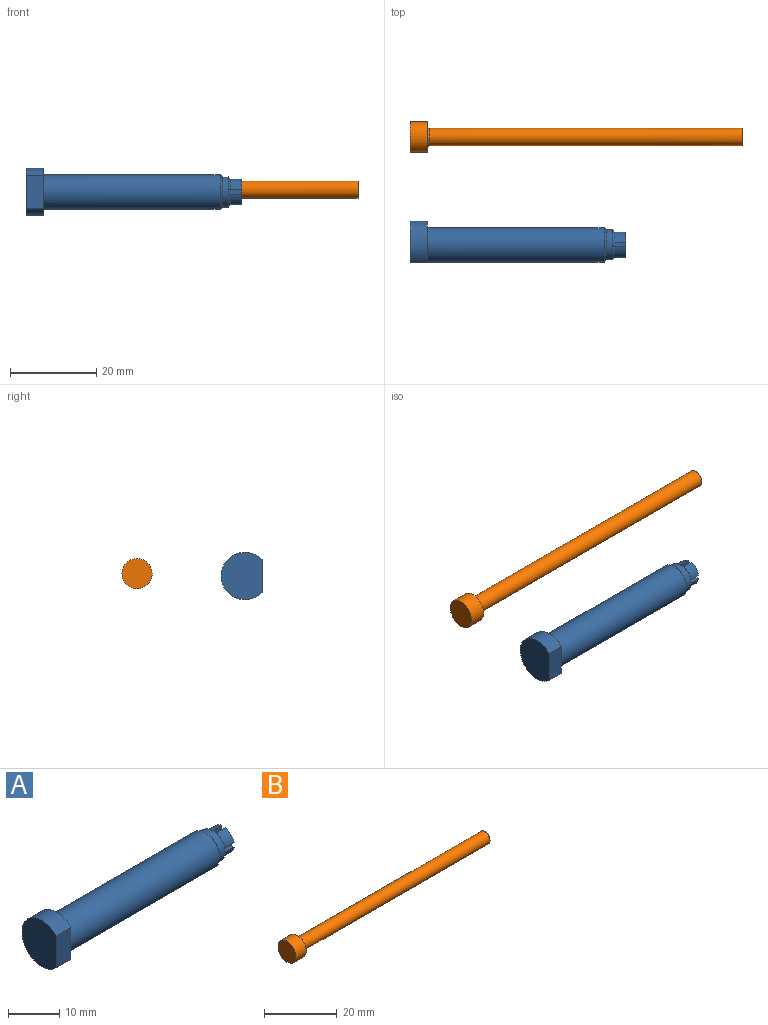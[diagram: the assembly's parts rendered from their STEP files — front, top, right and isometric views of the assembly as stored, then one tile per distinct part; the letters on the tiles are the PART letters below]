
ASSEMBLY  parts=2 mates=1
PART A: 32 faces, bbox 50x9.5x11 mm
  f0: cone r=3mm half-angle=45deg, axis (-1,0,0), area 2.9mm2, adj f1,f11,f21,f28
  f1: cylinder r=3mm len=2.5mm, axis (1,0,0), area 9.3mm2, adj f0,f14,f21,f28
  f2: cone r=3mm half-angle=45deg, axis (-1,0,0), area 2.9mm2, adj f3,f11,f18,f24
  f3: cylinder r=3mm len=2.5mm, axis (1,0,0), area 9.3mm2, adj f2,f14,f18,f24
  f4: cone r=3mm half-angle=45deg, axis (-1,0,0), area 2.9mm2, adj f5,f11,f16,f20
  f5: cylinder r=3mm len=2.5mm, axis (1,0,0), area 9.3mm2, adj f4,f14,f16,f20
  f6: plane 11x9.5mm, normal (-1,0,0), area 87.3mm2, adj f7,f15
  f7: cylinder r=5.5mm len=11mm, axis (1,0,0), area 104.9mm2, adj f6,f8,f15
  f8: plane 11x9.5mm, normal (1,0,0), area 37mm2, adj f7,f9,f15
  f9: cylinder r=4mm len=41mm, axis (1,0,0), area 1030.4mm2, adj f8,f10
  f10: cone r=3.5mm half-angle=45deg, axis (-1,0,0), area 16.7mm2, adj f9,f11
  f11: cylinder r=3.5mm len=7mm, axis (1,0,0), area 33mm2, adj f0,f2,f4,f10,f12,f19,f23,f27
  f12: cone r=3mm half-angle=45deg, axis (-1,0,0), area 2.9mm2, adj f11,f13,f26,f29
  f13: cylinder r=3mm len=2.5mm, axis (1,0,0), area 9.3mm2, adj f12,f14,f26,f29
  f14: plane 5.92x5.92mm, normal (1,0,0), area 24.3mm2, adj f1,f3,f5,f13,f16,f17,f18,f20
  f15: plane 7.55x4mm, normal (0,-1,0), area 30.2mm2, adj f6,f7,f8
  f16: plane 3.01x1.47mm, normal (0,-1,0), area 3mm2, adj f4,f5,f14,f17,f19
  f17: plane 3x1mm, normal (0,0,1), area 3mm2, adj f14,f16,f18,f19
  f18: plane 3.01x1.47mm, normal (0,1,0), area 3mm2, adj f2,f3,f14,f17,f19
  f19: plane 1.5x1mm, normal (1,0,0), area 1.5mm2, adj f11,f16,f17,f18
  f20: plane 3.01x1.47mm, normal (0,0,-1), area 3mm2, adj f4,f5,f14,f22,f23
  f21: plane 3.01x1.47mm, normal (0,0,1), area 3mm2, adj f0,f1,f14,f22,f23
  f22: plane 3x1mm, normal (0,1,0), area 3mm2, adj f14,f20,f21,f23
  f23: plane 1.5x1mm, normal (1,0,0), area 1.5mm2, adj f11,f20,f21,f22
  f24: plane 3.01x1.47mm, normal (0,0,-1), area 3mm2, adj f2,f3,f14,f25,f27
  f25: plane 3x1mm, normal (0,-1,0), area 3mm2, adj f14,f24,f26,f27
  f26: plane 3.01x1.47mm, normal (0,0,1), area 3mm2, adj f12,f13,f14,f25,f27
  f27: plane 1.5x1mm, normal (1,0,0), area 1.5mm2, adj f11,f24,f25,f26
  f28: plane 3.01x1.47mm, normal (0,-1,0), area 3mm2, adj f0,f1,f14,f30,f31
  f29: plane 3.01x1.47mm, normal (0,1,0), area 3mm2, adj f12,f13,f14,f30,f31
  f30: plane 3x1mm, normal (0,0,-1), area 3mm2, adj f14,f28,f29,f31
  f31: plane 1.5x1mm, normal (1,0,0), area 1.5mm2, adj f11,f28,f29,f30
PART B: 6 faces, bbox 77x7x7 mm
  f0: torus R=2.5mm, axis (-1,0,0), area 10.8mm2, adj f1,f2
  f1: cylinder r=2mm len=72.5mm, axis (1,0,0), area 911.1mm2, adj f0,f3
  f2: plane 7x7mm, normal (1,0,0), area 18.8mm2, adj f0,f4
  f3: plane 4x4mm, normal (1,0,0), area 12.6mm2, adj f1
  f4: cylinder r=3.5mm len=7mm, axis (1,0,0), area 88mm2, adj f2,f5
  f5: plane 7x7mm, normal (-1,0,0), area 38.5mm2, adj f4
PLACE A t=(-17.03,-24.59,-2.36)mm
PLACE B t=(-17.03,0.41,-1.81)mm
MATE planar B.f0 <-> A.f10  axis (-1,0,0) through (-17.03,0.41,-1.81)mm
